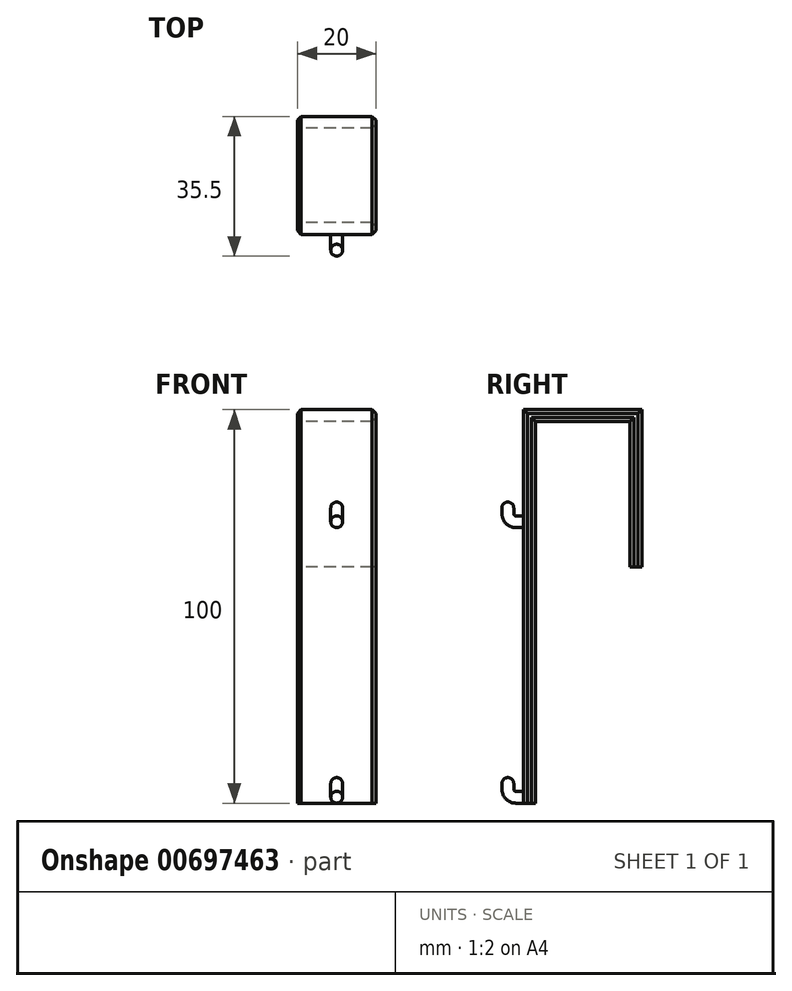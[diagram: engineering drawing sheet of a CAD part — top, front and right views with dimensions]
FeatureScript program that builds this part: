
annotation { "Feature Type Name" : "Feature", "Feature Type Description" : "" }
export const myFeature = defineFeature(function(context is Context, id is Id, definition is map)
    precondition{}
    {
        {
            var Q0;
            Q0=qCreatedBy(makeId("Right.planeOp"),FACE);
            var sketch = newSketch(context, id + "F0", { "sketchPlane" : qUnion([Q0])});
            skLineSegment(sketch, "E0.bottom", {"start": v(0, 0) * mm, "end": v(-30, 0) * mm});
            skLineSegment(sketch, "E0.left", {"start": v(0, 0) * mm, "end": v(0, -40) * mm});
            skLineSegment(sketch, "E0.right", {"start": v(-30, 0) * mm, "end": v(-30, -100) * mm});
            skLineSegment(sketch, "E1.bottom", {"start": v(-27, -3) * mm, "end": v(-3, -3) * mm});
            skLineSegment(sketch, "E1.left", {"start": v(-27, -3) * mm, "end": v(-27, -100) * mm});
            skLineSegment(sketch, "E1.right", {"start": v(-3, -3) * mm, "end": v(-3, -40) * mm});
            skLineSegment(sketch, "E2", {"start": v(-3, -40) * mm, "end": v(0, -40) * mm});
            skLineSegment(sketch, "E3.trimOffspring", {"start": v(-27, -100) * mm, "end": v(-30, -100) * mm});
            skSolve(sketch);
        }
        {
            var Q0;
            Q0=qSketchRegion(id+"F0",true);
            extrude(context, id + "F1", {"entities" : qUnion([Q0]), "endBound" : BoundingType.SYMMETRIC, "depth" : 20 * mm, "offsetDistance" : 25 * mm});
        }
        {
            var Q0;
            Q0=qCreatedBy(makeId("Right.planeOp"),FACE);
            var sketch = newSketch(context, id + "F2", { "sketchPlane" : qUnion([Q0])});
            skLineSegment(sketch, "E4", {"start": v(-30, -98.5) * mm, "end": v(-32, -98.5) * mm});
            skLineSegment(sketch, "E5", {"start": v(-34, -96.5) * mm, "end": v(-34, -93.5) * mm});
            skPoint(sketch, "E6.visualSharp", {"position": v(-34, -98.5) * mm});
            skArc(sketch, "E6.filletArc", {"start": v(-34, -96.5) * mm, "mid": v(-33.41, -97.91) * mm, "end": v(-32, -98.5) * mm});
            skSolve(sketch);
        }
        {
            var Q0;
            Q0=makeQuery(id+"F1.opExtrude","SWEPT_FACE",FACE,{"disambiguationData":[OSD([sQuery(id+"F0.wireOp",EDGE,"E0.right")])]});
            var sketch = newSketch(context, id + "F3", { "sketchPlane" : qUnion([Q0])});
            skCircle(sketch, "E7", {"center": v(0, -98.5) * mm, "radius": 1.5 * mm});
            skSolve(sketch);
        }
        {
            var Q0;
            Q0=qSketchRegion(id+"F3",true);
            var Q1;
            Q1=qConstructionFilter(qBodyType(qCreatedBy(id+"F2",EDGE),BodyType.WIRE),ConstructionObject.NO);
            sweep(context, id + "F4", {"operationType" : NewBodyOperationType.ADD, "profiles" : qUnion([Q0]), "path" : qUnion([Q1])});
        }
        {
            var Q0;
            Q0=makeQuery(id+"F4.opSweep","CAP_EDGE",EDGE,{"disambiguationData":[OSD([sQuery(id+"F2.wireOp",VERTEX,"E5.end"),sQuery(id+"F3.wireOp",EDGE,"E7")])],"isStart":false});
            var Q1;
            Q1=makeQuery(id+"F4.opSweep","CAP_EDGE",EDGE,{"disambiguationData":[OSD([sQuery(id+"F2.wireOp",VERTEX,"E4.start"),sQuery(id+"F3.wireOp",EDGE,"E7")])],"isStart":true});
            fillet(context, id + "F5", {"entities" : qUnion([Q0, Q1]), "radius" : 1.5 * mm, "tangentPropagation" : true, "allowEdgeOverflow" : false});
        }
        {
            var Q0;
            Q0=qCreatedBy(makeId("Right.planeOp"),FACE);
            var sketch = newSketch(context, id + "F6", { "sketchPlane" : qUnion([Q0])});
            skLineSegment(sketch, "E8", {"start": v(-34, -23.5) * mm, "end": v(-34, -26.5) * mm});
            skLineSegment(sketch, "E9", {"start": v(-32, -28.5) * mm, "end": v(-30, -28.5) * mm});
            skPoint(sketch, "E10.visualSharp", {"position": v(-34, -28.5) * mm});
            skArc(sketch, "E10.filletArc", {"start": v(-34, -26.5) * mm, "mid": v(-33.41, -27.91) * mm, "end": v(-32, -28.5) * mm});
            skSolve(sketch);
        }
        {
            var Q0;
            Q0=makeQuery(id+"F1.opExtrude","SWEPT_FACE",FACE,{"disambiguationData":[OSD([sQuery(id+"F0.wireOp",EDGE,"E0.right")])]});
            var sketch = newSketch(context, id + "F7", { "sketchPlane" : qUnion([Q0])});
            skCircle(sketch, "E11", {"center": v(0, -28.5) * mm, "radius": 1.5 * mm});
            skSolve(sketch);
        }
        {
            var Q0;
            Q0=qSketchRegion(id+"F7",true);
            var Q1;
            Q1=qConstructionFilter(qBodyType(qCreatedBy(id+"F6",EDGE),BodyType.WIRE),ConstructionObject.NO);
            sweep(context, id + "F8", {"operationType" : NewBodyOperationType.ADD, "profiles" : qUnion([Q0]), "path" : qUnion([Q1])});
        }
        {
            var Q0;
            Q0=makeQuery(id+"F8.opSweep","CAP_EDGE",EDGE,{"disambiguationData":[OSD([sQuery(id+"F6.wireOp",VERTEX,"E8.start"),sQuery(id+"F7.wireOp",EDGE,"E11")])],"isStart":false});
            fillet(context, id + "F9", {"entities" : qUnion([Q0]), "radius" : 1.5 * mm, "tangentPropagation" : true, "allowEdgeOverflow" : false});
        }
        {
            var Q0;
            Q0=makeQuery(id+"F1.opExtrude","CAP_EDGE",EDGE,{"disambiguationData":[OSD([sQuery(id+"F0.wireOp",EDGE,"E0.right")])],"isStart":false});
            var Q1;
            Q1=makeQuery(id+"F1.opExtrude","CAP_EDGE",EDGE,{"disambiguationData":[OSD([sQuery(id+"F0.wireOp",EDGE,"E0.bottom")])],"isStart":false});
            var Q2;
            Q2=makeQuery(id+"F1.opExtrude","CAP_EDGE",EDGE,{"disambiguationData":[OSD([sQuery(id+"F0.wireOp",EDGE,"E0.left")])],"isStart":false});
            var Q3;
            Q3=makeQuery(id+"F1.opExtrude","CAP_EDGE",EDGE,{"disambiguationData":[OSD([sQuery(id+"F0.wireOp",EDGE,"E1.right")])],"isStart":false});
            var Q4;
            Q4=makeQuery(id+"F1.opExtrude","CAP_EDGE",EDGE,{"disambiguationData":[OSD([sQuery(id+"F0.wireOp",EDGE,"E1.bottom")])],"isStart":false});
            var Q5;
            Q5=makeQuery(id+"F1.opExtrude","CAP_EDGE",EDGE,{"disambiguationData":[OSD([sQuery(id+"F0.wireOp",EDGE,"E1.left")])],"isStart":false});
            var Q6;
            Q6=makeQuery(id+"F1.opExtrude","CAP_EDGE",EDGE,{"disambiguationData":[OSD([sQuery(id+"F0.wireOp",EDGE,"E0.right")])],"isStart":true});
            var Q7;
            Q7=makeQuery(id+"F1.opExtrude","CAP_EDGE",EDGE,{"disambiguationData":[OSD([sQuery(id+"F0.wireOp",EDGE,"E1.left")])],"isStart":true});
            var Q8;
            Q8=makeQuery(id+"F1.opExtrude","CAP_EDGE",EDGE,{"disambiguationData":[OSD([sQuery(id+"F0.wireOp",EDGE,"E0.bottom")])],"isStart":true});
            var Q9;
            Q9=makeQuery(id+"F1.opExtrude","CAP_EDGE",EDGE,{"disambiguationData":[OSD([sQuery(id+"F0.wireOp",EDGE,"E1.bottom")])],"isStart":true});
            var Q10;
            Q10=makeQuery(id+"F1.opExtrude","CAP_EDGE",EDGE,{"disambiguationData":[OSD([sQuery(id+"F0.wireOp",EDGE,"E1.right")])],"isStart":true});
            var Q11;
            Q11=makeQuery(id+"F1.opExtrude","CAP_EDGE",EDGE,{"disambiguationData":[OSD([sQuery(id+"F0.wireOp",EDGE,"E0.left")])],"isStart":true});
            chamfer(context, id + "F10", {"entities" : qUnion([Q0, Q1, Q2, Q3, Q4, Q5, Q6, Q7, Q8, Q9, Q10, Q11]), "width" : 1 * mm, "tangentPropagation" : true});
        }
    });
